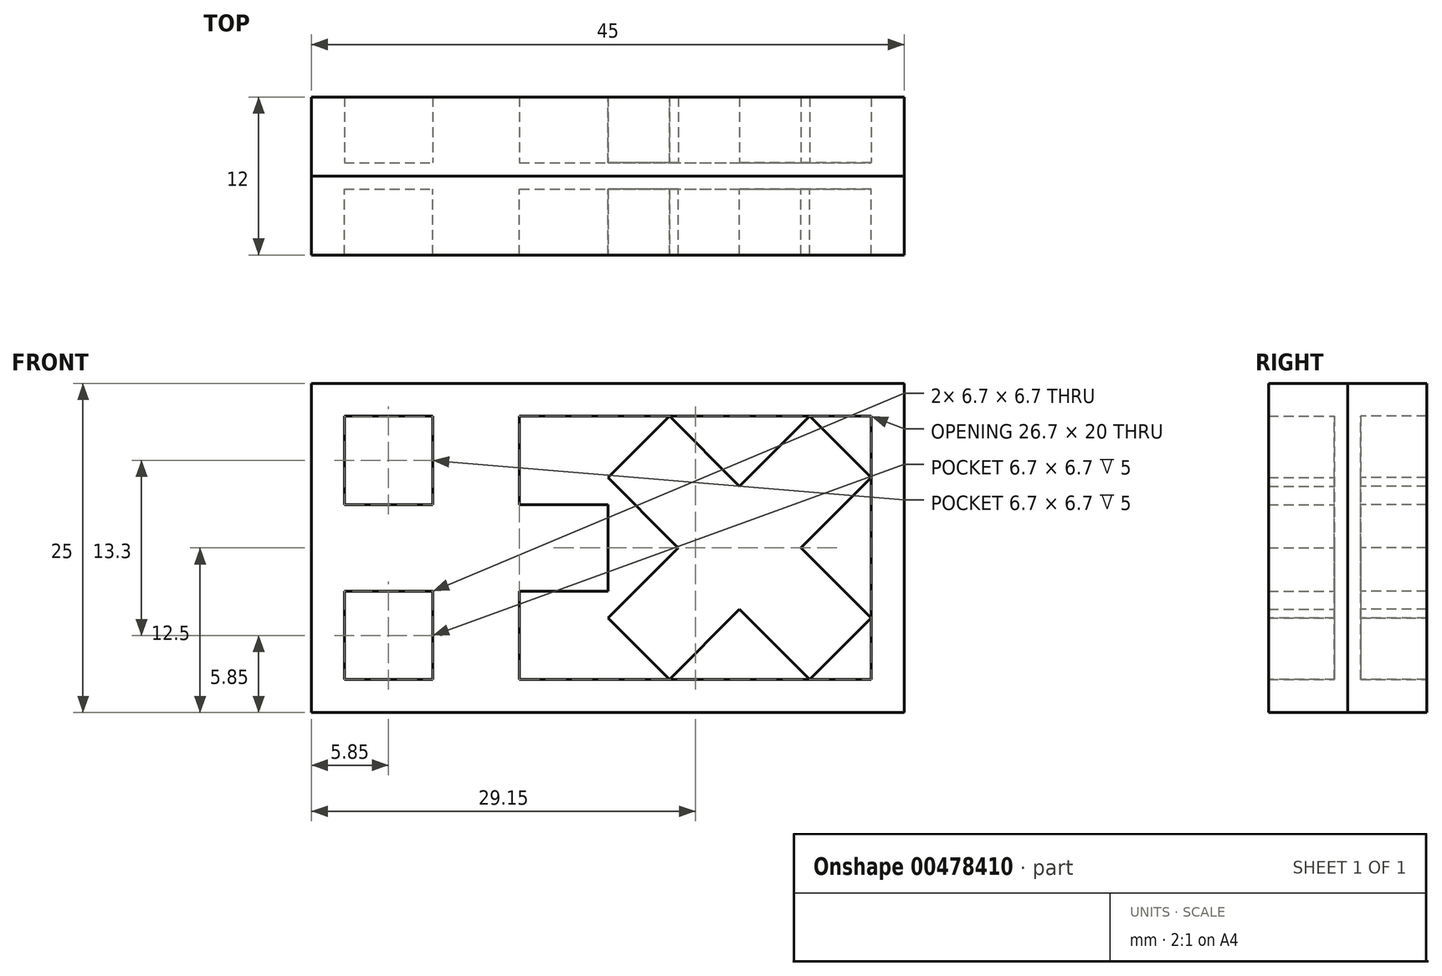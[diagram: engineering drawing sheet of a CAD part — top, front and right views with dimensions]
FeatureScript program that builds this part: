
annotation { "Feature Type Name" : "Feature", "Feature Type Description" : "" }
export const myFeature = defineFeature(function(context is Context, id is Id, definition is map)
    precondition{}
    {
        {
            var Q0;
            Q0=qCreatedBy(makeId("Front.planeOp"),FACE);
            var sketch = newSketch(context, id + "F0", { "sketchPlane" : qUnion([Q0])});
            skLineSegment(sketch, "E0.bottom", {"start": v(-22.5, 12.5) * mm, "end": v(22.5, 12.5) * mm});
            skLineSegment(sketch, "E0.top", {"start": v(-22.5, -12.5) * mm, "end": v(22.5, -12.5) * mm});
            skLineSegment(sketch, "E0.left", {"start": v(-22.5, 12.5) * mm, "end": v(-22.5, -12.5) * mm});
            skLineSegment(sketch, "E0.right", {"start": v(22.5, 12.5) * mm, "end": v(22.5, -12.5) * mm});
            skPoint(sketch, "E0.middle", {"position": v(0, 0) * mm});
            skSolve(sketch);
        }
        {
            var Q0;
            Q0 = qSketchRegion(id + "F0", true);
            extrude(context, id + "F1", {"entities" : qUnion([Q0]), "depth" : 1 * mm});
        }
        {
            var Q0;
            Q0=makeQuery(id+"F1.opExtrude","CAP_FACE",FACE,{"disambiguationData":[OSD([sQuery(id+"F0.wireOp",EDGE,"E0.bottom"),sQuery(id+"F0.wireOp",EDGE,"E0.top"),sQuery(id+"F0.wireOp",EDGE,"E0.left"),sQuery(id+"F0.wireOp",EDGE,"E0.right")])],"isStart":false});
            var sketch = newSketch(context, id + "F2", { "sketchPlane" : qUnion([Q0])});
            skLineSegment(sketch, "E1", {"start": v(-22.5, 12.5) * mm, "end": v(22.5, 12.5) * mm});
            skLineSegment(sketch, "E2", {"start": v(22.5, 12.5) * mm, "end": v(22.5, -12.5) * mm});
            skLineSegment(sketch, "E3", {"start": v(22.5, -12.5) * mm, "end": v(-22.5, -12.5) * mm});
            skLineSegment(sketch, "E4", {"start": v(-22.5, -12.5) * mm, "end": v(-22.5, 12.5) * mm});
            skLineSegment(sketch, "E5.bottom", {"start": v(-20, 10) * mm, "end": v(20, 10) * mm});
            skLineSegment(sketch, "E5.top", {"start": v(-20, -10) * mm, "end": v(20, -10) * mm});
            skLineSegment(sketch, "E5.left", {"start": v(-20, 10) * mm, "end": v(-20, -10) * mm});
            skLineSegment(sketch, "E5.right", {"start": v(20, 10) * mm, "end": v(20, -10) * mm});
            skPoint(sketch, "E5.middle", {"position": v(0, 0) * mm});
            skLineSegment(sketch, "E6", {"start": v(-20, 10) * mm, "end": v(0, -10) * mm, "construction": true});
            skLineSegment(sketch, "E7", {"start": v(0, -10) * mm, "end": v(20, 10) * mm, "construction": true});
            skLineSegment(sketch, "E8", {"start": v(-20, -10) * mm, "end": v(0, 10) * mm, "construction": true});
            skLineSegment(sketch, "E9", {"start": v(0, 10) * mm, "end": v(20, -10) * mm, "construction": true});
            skLineSegment(sketch, "E10", {"start": v(-10, 0) * mm, "end": v(-10, 10) * mm, "construction": true});
            skLineSegment(sketch, "E11", {"start": v(-10, 0) * mm, "end": v(0, 0) * mm, "construction": true});
            skLineSegment(sketch, "E12", {"start": v(-10, 8.35) * mm, "end": v(-6.7, 8.35) * mm, "construction": true});
            skLineSegment(sketch, "E13", {"start": v(-10, 8.35) * mm, "end": v(-13.3, 8.35) * mm, "construction": true});
            skLineSegment(sketch, "E14", {"start": v(-13.3, 10) * mm, "end": v(-13.3, 3.3) * mm});
            skLineSegment(sketch, "E15", {"start": v(-6.7, 10) * mm, "end": v(-6.7, 3.3) * mm});
            skLineSegment(sketch, "E16", {"start": v(-13.3, -3.3) * mm, "end": v(-20, -3.3) * mm});
            skLineSegment(sketch, "E17", {"start": v(-13.3, 3.3) * mm, "end": v(-20, 3.3) * mm});
            skLineSegment(sketch, "E18", {"start": v(-6.7, 3.3) * mm, "end": v(0, 3.3) * mm});
            skLineSegment(sketch, "E19", {"start": v(0, 3.3) * mm, "end": v(0, 0) * mm});
            skLineSegment(sketch, "E20", {"start": v(-6.7, -3.3) * mm, "end": v(0, -3.3) * mm});
            skLineSegment(sketch, "E21", {"start": v(0, -3.3) * mm, "end": v(0, 0) * mm});
            skLineSegment(sketch, "E22.trimOffspring", {"start": v(-6.7, -3.3) * mm, "end": v(-6.7, -10) * mm});
            skLineSegment(sketch, "E23.trimOffspring", {"start": v(-13.3, -3.3) * mm, "end": v(-13.3, -10) * mm});
            skLineSegment(sketch, "E24", {"start": v(7.33, 2.67) * mm, "end": v(5, 0.33) * mm, "construction": true});
            skLineSegment(sketch, "E25", {"start": v(7.33, 2.67) * mm, "end": v(9.67, 5) * mm, "construction": true});
            skLineSegment(sketch, "E26", {"start": v(5, 0.33) * mm, "end": v(0, 5.33) * mm});
            skLineSegment(sketch, "E27", {"start": v(0, 5.33) * mm, "end": v(4.67, 10) * mm});
            skLineSegment(sketch, "E28", {"start": v(4.67, 10) * mm, "end": v(9.67, 5) * mm});
            skLineSegment(sketch, "E29", {"start": v(9.67, 5) * mm, "end": v(10, 4.67) * mm});
            skLineSegment(sketch, "E30", {"start": v(2.33, -7.67) * mm, "end": v(4.67, -10) * mm, "construction": true});
            skLineSegment(sketch, "E31", {"start": v(2.33, -7.67) * mm, "end": v(0, -5.33) * mm, "construction": true});
            skLineSegment(sketch, "E32", {"start": v(0, -5.33) * mm, "end": v(0, -5.33) * mm});
            skLineSegment(sketch, "E33", {"start": v(0, -5.33) * mm, "end": v(4.67, -10) * mm});
            skLineSegment(sketch, "E34", {"start": v(4.67, -10) * mm, "end": v(4.67, -10) * mm});
            skLineSegment(sketch, "E35", {"start": v(4.67, -10) * mm, "end": v(10, -4.67) * mm});
            skLineSegment(sketch, "E36", {"start": v(20, 5.33) * mm, "end": v(15.33, 10) * mm});
            skLineSegment(sketch, "E37", {"start": v(15.33, 10) * mm, "end": v(10, 4.67) * mm});
            skLineSegment(sketch, "E38.trimOffspring", {"start": v(5.33, 0) * mm, "end": v(5, 0.33) * mm});
            skLineSegment(sketch, "E39.trimOffspring", {"start": v(5.33, 0) * mm, "end": v(0, -5.33) * mm});
            skLineSegment(sketch, "E40.trimOffspring", {"start": v(14.67, 0) * mm, "end": v(20, 5.33) * mm});
            skLineSegment(sketch, "E41", {"start": v(10, -4.67) * mm, "end": v(15.33, -10) * mm});
            skLineSegment(sketch, "E42", {"start": v(15.33, -10) * mm, "end": v(20, -5.33) * mm});
            skLineSegment(sketch, "E43", {"start": v(20, -5.33) * mm, "end": v(14.67, 0) * mm});
            skSolve(sketch);
        }
        {
            var Q0;
            Q0=makeQuery(id+"F2.imprint","IMPRINT",FACE,{"disambiguationData":[TD([[makeQuery(id+"F2.imprint","IMPRINT",EDGE,{"derivedFrom":sQuery(id+"F2.wireOp",EDGE,"E1")}),-1.0]])]});
            extrude(context, id + "F3", {"entities" : qUnion([Q0]), "operationType" : NewBodyOperationType.ADD, "depth" : 5 * mm});
        }
        {
            var Q0;
            {var subQ2=sQuery(id+"F2.wireOp",EDGE,"E14");Q0=makeQuery(id+"F2.imprint","IMPRINT",FACE,{"disambiguationData":[TD([[makeQuery(id+"F2.imprint","IMPRINT",EDGE,{"derivedFrom":subQ2}),1.0]])]});}
            extrude(context, id + "F4", {"entities" : qUnion([Q0]), "operationType" : NewBodyOperationType.ADD, "depth" : 5 * mm});
        }
        {
            var Q0;
            Q0=makeQuery(id+"F2.imprint","IMPRINT",FACE,{"disambiguationData":[TD([[makeQuery(id+"F2.imprint","IMPRINT",EDGE,{"derivedFrom":sQuery(id+"F2.wireOp",EDGE,"E26")}),-1.0]])]});
            extrude(context, id + "F5", {"entities" : qUnion([Q0]), "depth" : 5 * mm});
        }
        {
            var Q0;
            Q0=makeQuery(id+"F1.opExtrude","SWEPT_BODY",BODY,{"disambiguationData":[OSD([sQuery(id+"F0.wireOp",EDGE,"E0.bottom"),sQuery(id+"F0.wireOp",EDGE,"E0.top"),sQuery(id+"F0.wireOp",EDGE,"E0.left"),sQuery(id+"F0.wireOp",EDGE,"E0.right")])]});
            var Q1;
            Q1=makeQuery(id+"F5.opExtrude","SWEPT_BODY",BODY,{"disambiguationData":[OSD([sQuery(id+"F2.wireOp",EDGE,"E26"),sQuery(id+"F2.wireOp",EDGE,"E27"),sQuery(id+"F2.wireOp",EDGE,"E28"),sQuery(id+"F2.wireOp",EDGE,"E29"),sQuery(id+"F2.wireOp",EDGE,"E33"),sQuery(id+"F2.wireOp",EDGE,"E35"),sQuery(id+"F2.wireOp",EDGE,"E36"),sQuery(id+"F2.wireOp",EDGE,"E37"),sQuery(id+"F2.wireOp",EDGE,"E38.trimOffspring"),sQuery(id+"F2.wireOp",EDGE,"E39.trimOffspring"),sQuery(id+"F2.wireOp",EDGE,"E40.trimOffspring"),sQuery(id+"F2.wireOp",EDGE,"E41"),sQuery(id+"F2.wireOp",EDGE,"E42"),sQuery(id+"F2.wireOp",EDGE,"E43")])]});
            var Q2;
            Q2=qCreatedBy(makeId("Front.planeOp"),FACE);
            mirror(context, id + "F6", {"entities" : qUnion([Q0, Q1]), "mirrorPlane" : qUnion([Q2])});
        }
    });
